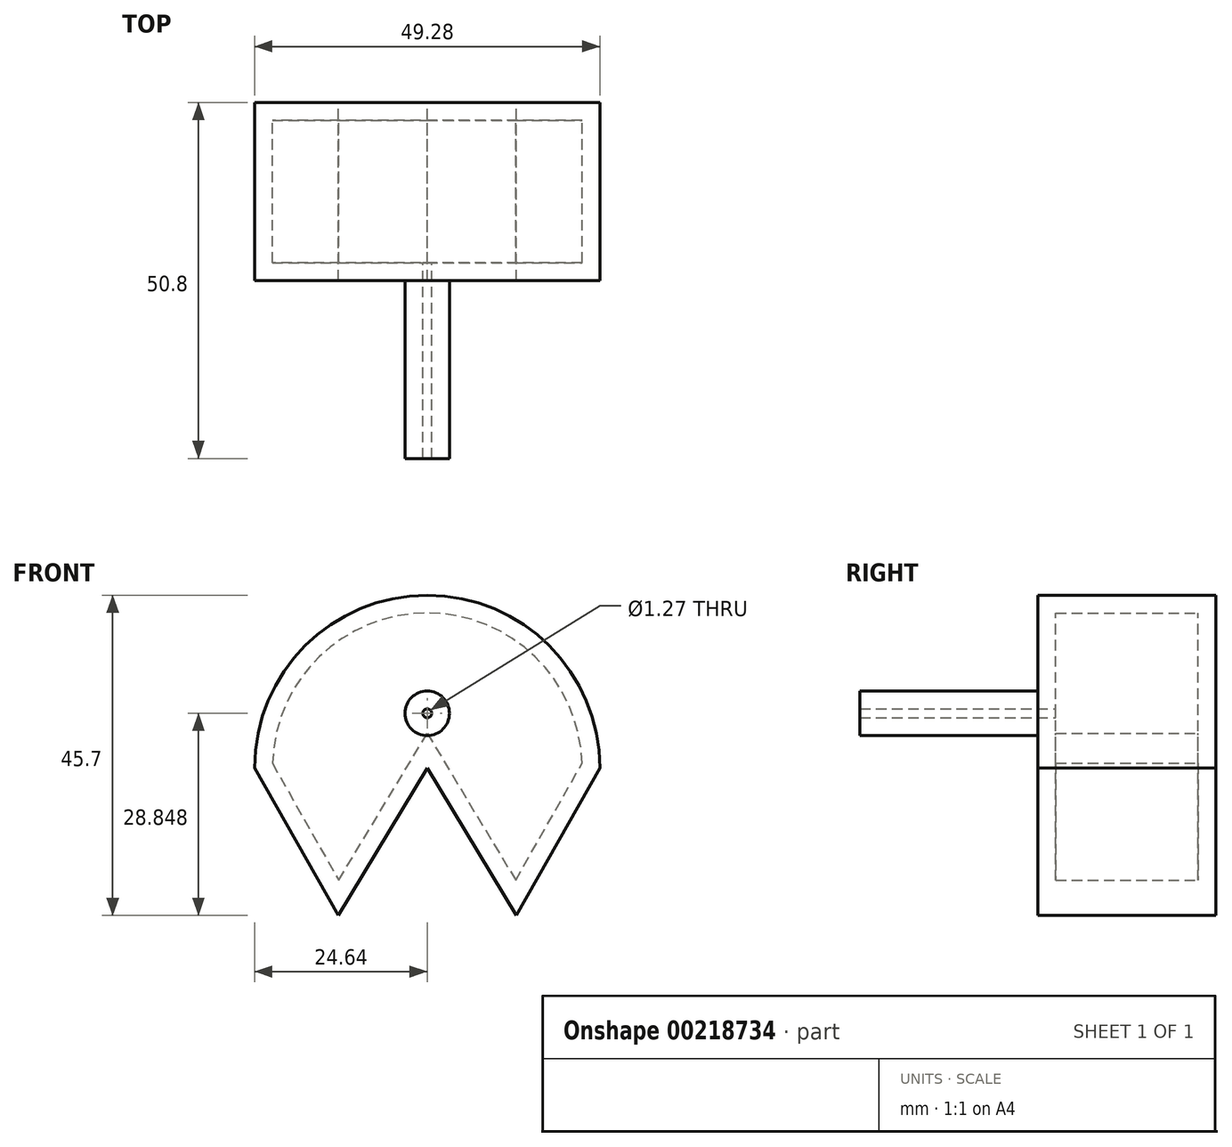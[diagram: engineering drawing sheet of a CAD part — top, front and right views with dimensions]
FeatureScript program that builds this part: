
annotation { "Feature Type Name" : "Feature", "Feature Type Description" : "" }
export const myFeature = defineFeature(function(context is Context, id is Id, definition is map)
    precondition{}
    {
        {
            var Q0;
            Q0=qCreatedBy(makeId("Front.planeOp"),FACE);
            var sketch = newSketch(context, id + "F0", { "sketchPlane" : qUnion([Q0])});
            skArc(sketch, "E0", {"start": v(0, 24.64) * mm, "mid": v(-17.42, 17.42) * mm, "end": v(-24.64, 0) * mm});
            skArc(sketch, "E1", {"start": v(24.64, 0) * mm, "mid": v(17.42, 17.42) * mm, "end": v(0, 24.64) * mm});
            skLineSegment(sketch, "E2", {"start": v(-24.64, 0) * mm, "end": v(-12.7, -21.06) * mm});
            skLineSegment(sketch, "E3", {"start": v(-12.7, -21.06) * mm, "end": v(0, 0) * mm});
            skLineSegment(sketch, "E4", {"start": v(0, 0) * mm, "end": v(12.7, -21.06) * mm});
            skLineSegment(sketch, "E5", {"start": v(12.7, -21.06) * mm, "end": v(24.64, 0) * mm});
            skSolve(sketch);
        }
        {
            var Q0;
            Q0 = qSketchRegion(id + "F0", true);
            extrude(context, id + "F1", {"entities" : qUnion([Q0]), "depth" : 25.4 * mm});
        }
        {
            var Q0;
            Q0=makeQuery(id+"F1.opExtrude","CAP_FACE",FACE,{"disambiguationData":[OSD([sQuery(id+"F0.wireOp",EDGE,"E0"),sQuery(id+"F0.wireOp",EDGE,"E1"),sQuery(id+"F0.wireOp",EDGE,"E2"),sQuery(id+"F0.wireOp",EDGE,"E3"),sQuery(id+"F0.wireOp",EDGE,"E4"),sQuery(id+"F0.wireOp",EDGE,"E5")])],"isStart":false});
            var sketch = newSketch(context, id + "F2", { "sketchPlane" : qUnion([Q0])});
            skCircle(sketch, "E6", {"center": v(0, 7.79) * mm, "radius": 3.18 * mm});
            skSolve(sketch);
        }
        {
            var Q0;
            Q0 = qSketchRegion(id + "F2", true);
            extrude(context, id + "F3", {"entities" : qUnion([Q0]), "operationType" : NewBodyOperationType.ADD, "depth" : 25.4 * mm});
        }
        {
            var Q0;
            Q0=makeQuery(id+"F3.opExtrude","CAP_FACE",FACE,{"disambiguationData":[OSD([sQuery(id+"F2.wireOp",EDGE,"E6")])],"isStart":false});
            shell(context, id + "F4", {"entities" : qUnion([Q0]), "thickness" : 2.54 * mm});
        }
    });
